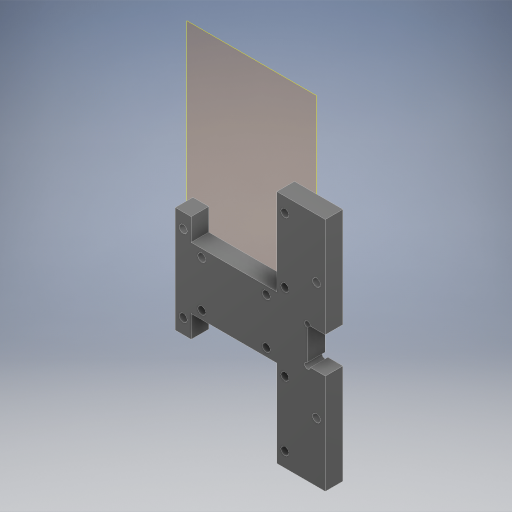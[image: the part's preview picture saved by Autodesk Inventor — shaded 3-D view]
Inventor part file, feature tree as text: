
AUTODESK INVENTOR PART (.ipt)
format: ipt  version: 2024 (Build 280153000, 153)  size: 403,968 bytes
history: native  units: in
note: dims shown in document units (in); Inventor stores cm internally (conversion verified against a paired STEP export)
features: other x5, extrude x2, sketch x2, reference x2
ambient origin geometry x8: Origin, YZ Plane, XZ Plane, XY Plane, X Axis, Y Axis, Z Axis, Center Point
bodies: Body1 (feature_tree)
feature tree (11):
  other  "작업 평면1"
  extrude  "돌출5"  Depth=0.0039in
  extrude  "돌출6"  Depth=0.1969in
  sketch  "스케치1"
  reference  "참조1"
  reference  "참조2"
  sketch  "스케치2"
  other  "조립품13"
  other  "MX-64T+idle.ipt:3"
  other  "MX-64T:1"
  other  "MX-64T+idle.ipt:2"
